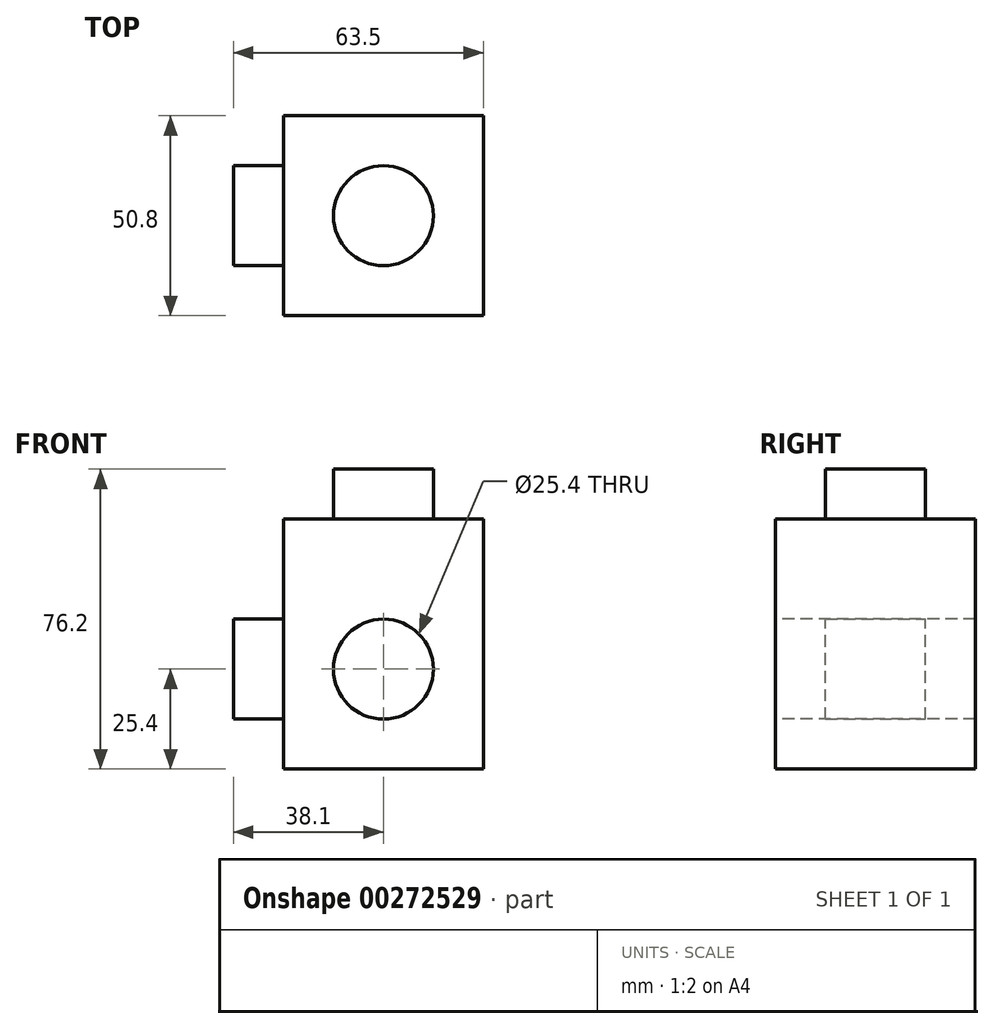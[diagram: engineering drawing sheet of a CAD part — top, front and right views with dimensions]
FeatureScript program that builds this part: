
annotation { "Feature Type Name" : "Feature", "Feature Type Description" : "" }
export const myFeature = defineFeature(function(context is Context, id is Id, definition is map)
    precondition{}
    {
        {
            var Q0;
            Q0=qCreatedBy(makeId("Front.planeOp"),FACE);
            var sketch = newSketch(context, id + "F0", { "sketchPlane" : qUnion([Q0])});
            skLineSegment(sketch, "E0.bottom", {"start": v(0, 0) * mm, "end": v(-50.8, 0) * mm});
            skLineSegment(sketch, "E0.top", {"start": v(0, 50.8) * mm, "end": v(-50.8, 50.8) * mm});
            skLineSegment(sketch, "E0.left", {"start": v(0, 0) * mm, "end": v(0, 50.8) * mm});
            skLineSegment(sketch, "E0.right", {"start": v(-50.8, 0) * mm, "end": v(-50.8, 50.8) * mm});
            skSolve(sketch);
        }
        {
            var Q0;
            Q0 = qSketchRegion(id + "F0", true);
            extrude(context, id + "F1", {"entities" : qUnion([Q0]), "depth" : 50.8 * mm});
        }
        {
            var Q0;
            Q0=makeQuery(id+"F1.opExtrude","CAP_FACE",FACE,{"disambiguationData":[OSD([sQuery(id+"F0.wireOp",EDGE,"E0.bottom"),sQuery(id+"F0.wireOp",EDGE,"E0.top"),sQuery(id+"F0.wireOp",EDGE,"E0.left"),sQuery(id+"F0.wireOp",EDGE,"E0.right")])],"isStart":false});
            var sketch = newSketch(context, id + "F2", { "sketchPlane" : qUnion([Q0])});
            skCircle(sketch, "E1", {"center": v(-25.4, 25.4) * mm, "radius": 12.7 * mm});
            skSolve(sketch);
        }
        {
            var Q0;
            Q0 = qSketchRegion(id + "F2", true);
            extrude(context, id + "F3", {"entities" : qUnion([Q0]), "operationType" : NewBodyOperationType.REMOVE, "oppositeDirection" : true, "depth" : 50.8 * mm});
        }
        {
            var Q0;
            Q0=makeQuery(id+"F1.opExtrude","SWEPT_FACE",FACE,{"disambiguationData":[OSD([sQuery(id+"F0.wireOp",EDGE,"E0.right")])]});
            var sketch = newSketch(context, id + "F4", { "sketchPlane" : qUnion([Q0])});
            skLineSegment(sketch, "E2.bottom", {"start": v(38.1, 12.7) * mm, "end": v(12.7, 12.7) * mm});
            skLineSegment(sketch, "E2.top", {"start": v(38.1, 38.1) * mm, "end": v(12.7, 38.1) * mm});
            skLineSegment(sketch, "E2.left", {"start": v(38.1, 12.7) * mm, "end": v(38.1, 38.1) * mm});
            skLineSegment(sketch, "E2.right", {"start": v(12.7, 12.7) * mm, "end": v(12.7, 38.1) * mm});
            skPoint(sketch, "E2.middle", {"position": v(25.4, 25.4) * mm});
            skSolve(sketch);
        }
        {
            var Q0;
            Q0=makeQuery(id+"F1.opExtrude","SWEPT_FACE",FACE,{"disambiguationData":[OSD([sQuery(id+"F0.wireOp",EDGE,"E0.top")])]});
            extrude(context, id + "F5", {"entities" : qUnion([Q0]), "operationType" : NewBodyOperationType.ADD, "depth" : 12.7 * mm});
        }
        {
            var Q0;
            Q0=makeQuery(id+"F5.opExtrude","CAP_FACE",FACE,{"disambiguationData":[OSD([sQuery(id+"F0.wireOp",EDGE,"E0.top")])],"isStart":false});
            var sketch = newSketch(context, id + "F6", { "sketchPlane" : qUnion([Q0])});
            skCircle(sketch, "E3", {"center": v(-25.4, -25.4) * mm, "radius": 12.7 * mm});
            skSolve(sketch);
        }
        {
            var Q0;
            Q0 = qSketchRegion(id + "F6", true);
            extrude(context, id + "F7", {"entities" : qUnion([Q0]), "operationType" : NewBodyOperationType.ADD, "depth" : 12.7 * mm});
        }
        {
            var Q0;
            Q0 = qSketchRegion(id + "F4", true);
            extrude(context, id + "F8", {"entities" : qUnion([Q0]), "operationType" : NewBodyOperationType.ADD, "depth" : 12.7 * mm});
        }
    });
